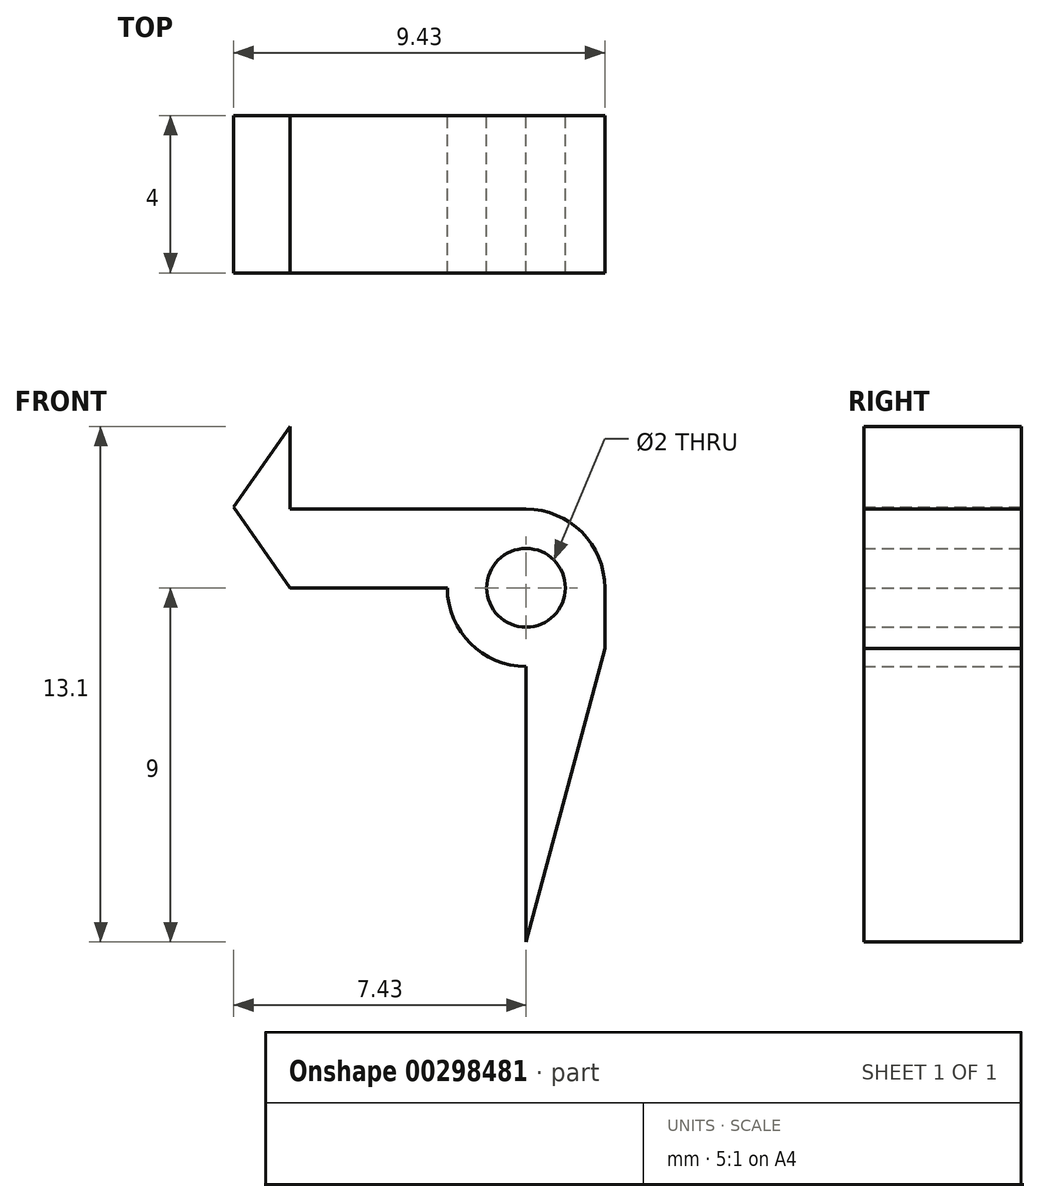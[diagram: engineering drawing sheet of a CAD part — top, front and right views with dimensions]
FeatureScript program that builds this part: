
annotation { "Feature Type Name" : "Feature", "Feature Type Description" : "" }
export const myFeature = defineFeature(function(context is Context, id is Id, definition is map)
    precondition{}
    {
        {
            var Q0;
            Q0=qCreatedBy(makeId("Front.planeOp"),FACE);
            var sketch = newSketch(context, id + "F0", { "sketchPlane" : qUnion([Q0])});
            skCircle(sketch, "E0", {"center": v(0, 0) * mm, "radius": 1 * mm});
            skCircle(sketch, "E1", {"center": v(0, 0) * mm, "radius": 2 * mm});
            skLineSegment(sketch, "E2", {"start": v(0, 2) * mm, "end": v(-6, 2) * mm});
            skLineSegment(sketch, "E3", {"start": v(2, 0) * mm, "end": v(2, -1.54) * mm});
            skLineSegment(sketch, "E4", {"start": v(0, -9) * mm, "end": v(0, -2) * mm});
            skLineSegment(sketch, "E5", {"start": v(-6, 4.1) * mm, "end": v(-7.43, 2.05) * mm});
            skLineSegment(sketch, "E6", {"start": v(-7.43, 2.05) * mm, "end": v(-6, 0) * mm});
            skLineSegment(sketch, "E7", {"start": v(-6, 0) * mm, "end": v(-2, 0) * mm});
            skLineSegment(sketch, "E8", {"start": v(-6, 2) * mm, "end": v(-6, 4.1) * mm});
            skLineSegment(sketch, "E9", {"start": v(0, -9) * mm, "end": v(2, -1.54) * mm});
            skSolve(sketch);
        }
        {
            var Q0;
            Q0 = qSketchRegion(id + "F0", true);
            extrude(context, id + "F1", {"entities" : qUnion([Q0]), "depth" : 4 * mm});
        }
    });
